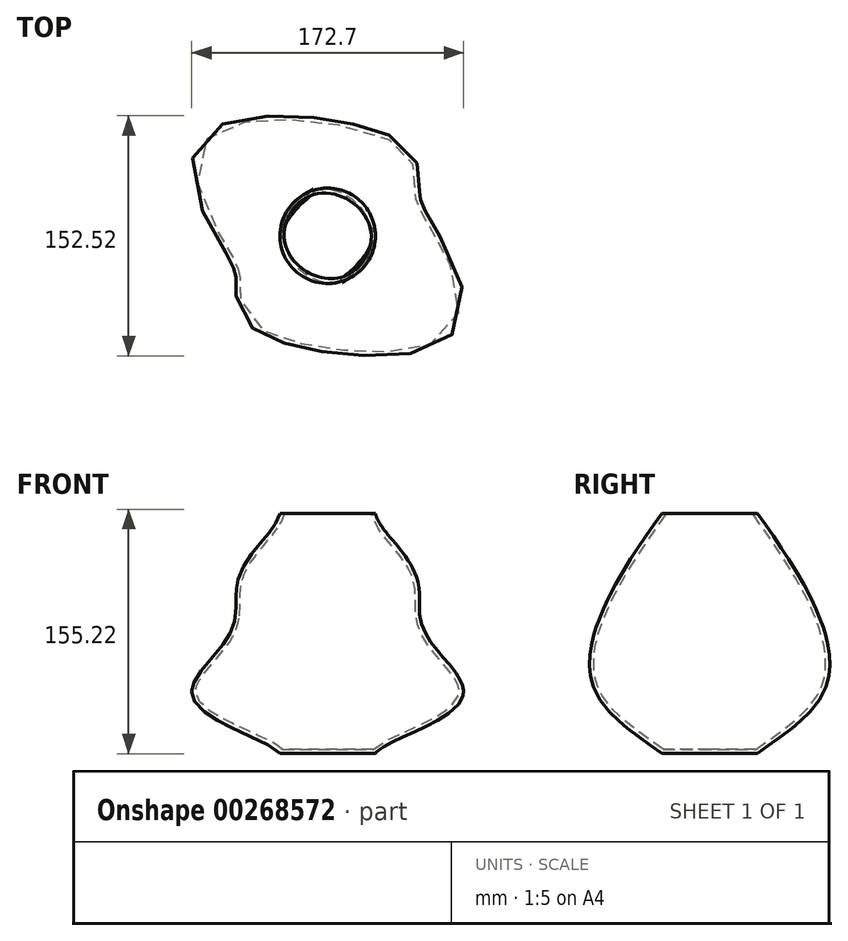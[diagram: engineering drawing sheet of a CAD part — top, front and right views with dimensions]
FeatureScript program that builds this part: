
annotation { "Feature Type Name" : "Feature", "Feature Type Description" : "" }
export const myFeature = defineFeature(function(context is Context, id is Id, definition is map)
    precondition{}
    {
        {
            var Q0;
            Q0=qCreatedBy(makeId("Top.planeOp"),FACE);
            var sketch = newSketch(context, id + "F0", { "sketchPlane" : qUnion([Q0])});
            skCircle(sketch, "E0", {"center": v(0, 0) * mm, "radius": 30.3 * mm});
            skSolve(sketch);
        }
        {
            var Q0;
            Q0=qCreatedBy(makeId("Top.planeOp"),FACE);
            cPlane(context, id + "F1", {"entities" : qUnion([Q0]), "cplaneType" : CPlaneType.OFFSET, "offset" : 38.1 * mm, "width" : 152.4 * mm, "height" : 152.4 * mm});
        }
        {
            var Q0;
            Q0=qCreatedBy(id+"F1.planeOp",FACE);
            var sketch = newSketch(context, id + "F2", { "sketchPlane" : qUnion([Q0])});
            skEllipse(sketch, "E1", {"center": v(0, 0) * mm, "majorRadius": 100.96 * mm, "minorRadius": 49.44 * mm, "majorAxis": v(-0.8, 0.6)});
            skSolve(sketch);
        }
        {
            var Q0;
            Q0=qCreatedBy(makeId("Top.planeOp"),FACE);
            cPlane(context, id + "F3", {"entities" : qUnion([Q0]), "cplaneType" : CPlaneType.OFFSET, "offset" : 101.6 * mm, "width" : 152.4 * mm, "height" : 152.4 * mm});
        }
        {
            var Q0;
            Q0=qCreatedBy(id+"F3.planeOp",FACE);
            var sketch = newSketch(context, id + "F4", { "sketchPlane" : qUnion([Q0])});
            skEllipse(sketch, "E2", {"center": v(0, 0) * mm, "majorRadius": 75.62 * mm, "minorRadius": 40.18 * mm, "majorAxis": v(0.66, 0.75)});
            skSolve(sketch);
        }
        {
            var Q0;
            Q0=qCreatedBy(makeId("Top.planeOp"),FACE);
            cPlane(context, id + "F5", {"entities" : qUnion([Q0]), "cplaneType" : CPlaneType.OFFSET, "offset" : 152.4 * mm, "width" : 152.4 * mm, "height" : 152.4 * mm});
        }
        {
            var Q0;
            Q0=qCreatedBy(id+"F5.planeOp",FACE);
            var sketch = newSketch(context, id + "F6", { "sketchPlane" : qUnion([Q0])});
            skCircle(sketch, "E3", {"center": v(0, 0) * mm, "radius": 30.3 * mm});
            skSolve(sketch);
        }
        {
            var Q0;
            Q0=makeQuery(id+"F0.imprint","IMPRINT",FACE,{"disambiguationData":[TD([[makeQuery(id+"F0.imprint","IMPRINT",EDGE,{"derivedFrom":sQuery(id+"F0.wireOp",EDGE,"E0")}),1.0]])]});
            var Q1;
            Q1=makeQuery(id+"F2.imprint","IMPRINT",FACE,{"disambiguationData":[TD([[makeQuery(id+"F2.imprint","IMPRINT",EDGE,{"derivedFrom":sQuery(id+"F2.wireOp",EDGE,"E1")}),1.0]])]});
            var Q2;
            Q2=makeQuery(id+"F4.imprint","IMPRINT",FACE,{"disambiguationData":[TD([[makeQuery(id+"F4.imprint","IMPRINT",EDGE,{"derivedFrom":sQuery(id+"F4.wireOp",EDGE,"E2")}),1.0]])]});
            var Q3;
            Q3=makeQuery(id+"F6.imprint","IMPRINT",FACE,{"disambiguationData":[TD([[makeQuery(id+"F6.imprint","IMPRINT",EDGE,{"derivedFrom":sQuery(id+"F6.wireOp",EDGE,"E3")}),1.0]])]});
            loft(context, id + "F7", {"sheetProfilesArray" : [{ "sheetProfileEntities" : qUnion([Q0]) }, { "sheetProfileEntities" : qUnion([Q1]) }, { "sheetProfileEntities" : qUnion([Q2]) }, { "sheetProfileEntities" : qUnion([Q3]) }]});
        }
        {
            var Q0;
            Q0=makeQuery(id+"F7.opLoft","CAP_FACE",FACE,{"disambiguationData":[OSD([makeQuery(id+"F6.imprint","IMPRINT",FACE,{"disambiguationData":[TD([[makeQuery(id+"F6.imprint","IMPRINT",EDGE,{"derivedFrom":sQuery(id+"F6.wireOp",EDGE,"E3")}),1.0]])]})])],"isStart":true});
            shell(context, id + "F8", {"entities" : qUnion([Q0]), "thickness" : 2.54 * mm});
        }
    });
